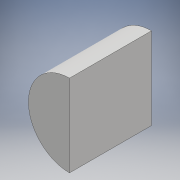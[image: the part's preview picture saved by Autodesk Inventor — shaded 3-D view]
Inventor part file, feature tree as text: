
AUTODESK INVENTOR PART (.ipt)
format: ipt  version: 2018 (Build 220112000, 112)  size: 87,552 bytes
history: native  units: mm
features: extrude x1, sketch x1
ambient origin geometry x8: Origin, YZ Plane, XZ Plane, XY Plane, X Axis, Y Axis, Z Axis, Center Point
bodies: Solid1 (feature_tree)
feature tree (2):
  extrude  "Extrusion1"  Depth=12.0mm TaperAngle=0.0deg
  sketch  "Sketch1"  dims[d0=12.0mm d1=12.0mm d2=0.0mm]
